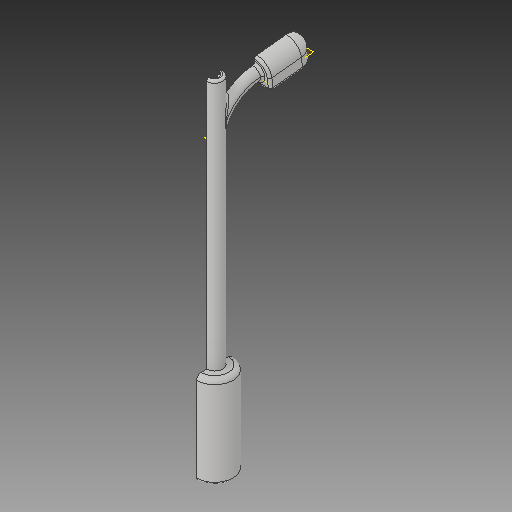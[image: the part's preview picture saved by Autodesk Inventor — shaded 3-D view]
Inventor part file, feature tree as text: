
AUTODESK INVENTOR PART (.ipt)
format: ipt  version: 2018 (Build 220112000, 112)  size: 399,872 bytes
history: native  units: in
note: dims shown in document units (in); Inventor stores cm internally (conversion verified against a paired STEP export)
features: sketch x10, other x3, plane x1
ambient origin geometry x8: Origin, YZ Plane, XZ Plane, XY Plane, X Axis, Y Axis, Z Axis, Center Point
bodies: Solid1 (feature_tree)
feature tree (14):
  other  "lampa.ipt"
  other  "Solid1::lampa.ipt"
  other  "TaggingFeature1"
  sketch  "Sketch1"  dims[d0=0.3937in]
  sketch  "Sketch6"
  sketch  "Sketch8"
  sketch  "Sketch9"
  sketch  "Sketch10"
  sketch  "Sketch11"
  sketch  "Sketch12"
  sketch  "Sketch13"
  sketch  "Sketch14"
  sketch  "Sketch15"
  plane  "Work Plane1"
